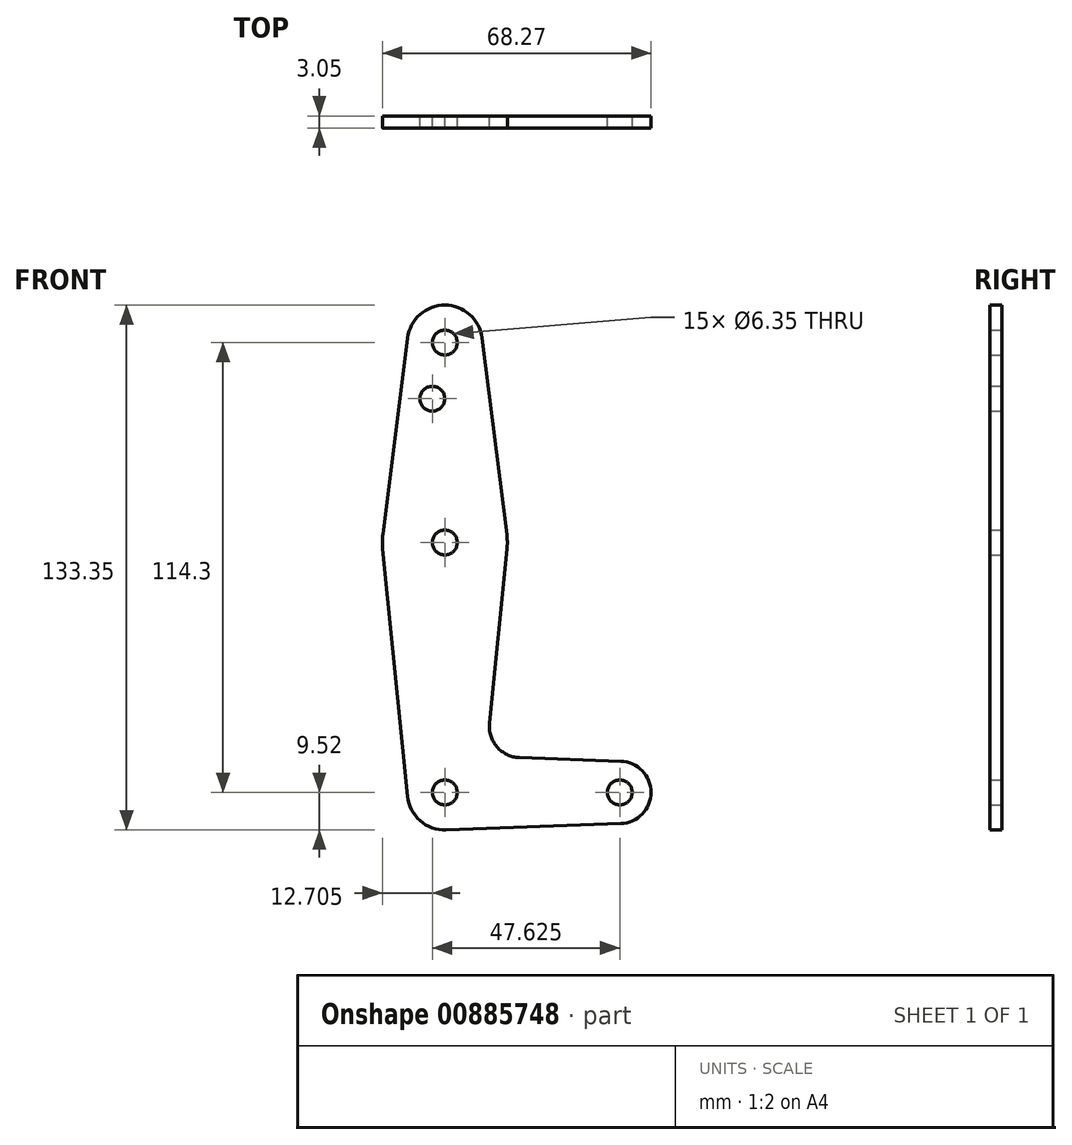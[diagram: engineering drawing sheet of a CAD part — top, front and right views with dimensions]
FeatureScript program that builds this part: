
annotation { "Feature Type Name" : "Feature", "Feature Type Description" : "" }
export const myFeature = defineFeature(function(context is Context, id is Id, definition is map)
    precondition{}
    {
        {
            var Q0;
            Q0=qCreatedBy(makeId("Front.planeOp"),FACE);
            var sketch = newSketch(context, id + "F0", { "sketchPlane" : qUnion([Q0])});
            skLineSegment(sketch, "E0", {"start": v(0, 114.3) * mm, "end": v(0, 0) * mm, "construction": true});
            skLineSegment(sketch, "E1", {"start": v(0, 0) * mm, "end": v(44.45, 0) * mm, "construction": true});
            skCircle(sketch, "E2", {"center": v(0, 114.3) * mm, "radius": 9.53 * mm});
            skCircle(sketch, "E3", {"center": v(0, 0) * mm, "radius": 9.53 * mm});
            skCircle(sketch, "E4", {"center": v(44.45, 0) * mm, "radius": 7.94 * mm});
            skCircle(sketch, "E5", {"center": v(0, 63.5) * mm, "radius": 15.88 * mm});
            skLineSegment(sketch, "E6", {"start": v(-15.75, 65.48) * mm, "end": v(-9.45, 115.5) * mm});
            skLineSegment(sketch, "E7", {"start": v(9.45, 115.5) * mm, "end": v(15.75, 65.48) * mm});
            skLineSegment(sketch, "E8", {"start": v(15.8, 61.91) * mm, "end": v(11.34, 17.6) * mm});
            skLineSegment(sketch, "E9", {"start": v(-15.8, 61.91) * mm, "end": v(-9.48, -0.95) * mm});
            skLineSegment(sketch, "E10", {"start": v(18.97, 8.85) * mm, "end": v(44.73, 7.93) * mm});
            skLineSegment(sketch, "E11", {"start": v(0.34, -9.52) * mm, "end": v(44.73, -7.93) * mm});
            skCircle(sketch, "E12", {"center": v(0, 114.3) * mm, "radius": 3.18 * mm});
            skCircle(sketch, "E13", {"center": v(0, 63.5) * mm, "radius": 3.18 * mm});
            skCircle(sketch, "E14", {"center": v(0, 0) * mm, "radius": 3.18 * mm});
            skCircle(sketch, "E15", {"center": v(44.45, 0) * mm, "radius": 3.18 * mm});
            skCircle(sketch, "E16", {"center": v(-3.17, 100.03) * mm, "radius": 3.18 * mm});
            skArc(sketch, "E17.filletArc", {"start": v(11.34, 17.6) * mm, "mid": v(13.26, 11.57) * mm, "end": v(18.97, 8.85) * mm});
            skSolve(sketch);
        }
        {
            var Q0;
            Q0 = qSketchRegion(id + "F0", true);
            extrude(context, id + "F1", {"entities" : qUnion([Q0]), "depth" : 3.05 * mm, "offsetDistance" : 25.4 * mm});
        }
    });
